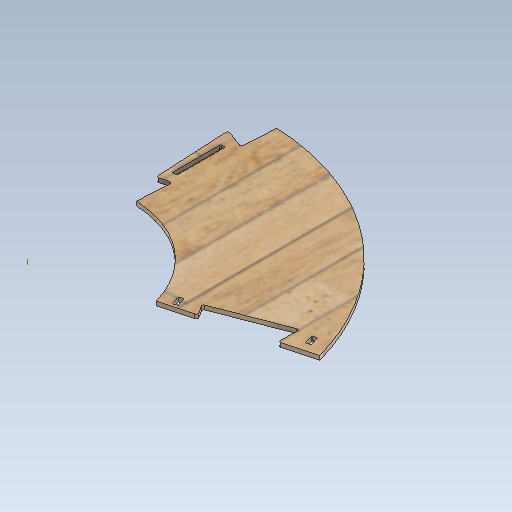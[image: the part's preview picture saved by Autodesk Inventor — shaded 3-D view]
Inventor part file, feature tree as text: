
AUTODESK INVENTOR PART (.ipt)
format: ipt  version: 2020 (Build 240168000, 168)  size: 463,360 bytes
history: native  units: mm
features: extrude x5, sketch x4, pattern_circular x3, mirror x1
ambient origin geometry x8: Origin, YZ Plane, XZ Plane, XY Plane, X Axis, Y Axis, Z Axis, Center Point
bodies: Body1 (feature_tree)
feature tree (13):
  extrude  "Extrusion3"  Depth=6.5mm
  extrude  "Extrusion4"  Depth=2.666667mm
  extrude  "Extrusion5"  Depth=1.333333mm
  sketch  "Sketch5"  dims[d32=1.333333mm d33=1.333333mm]
  extrude  "Extrusion7"  Depth=145.0mm
  pattern_circular  "Circular Pattern2"  Angle=90.0deg  [1 undecoded]
  pattern_circular  "Circular Pattern3"  [2 undecoded]
  mirror  "Mirror3"
  pattern_circular  "Circular Pattern4"  Angle=90.0deg  [1 undecoded]
  extrude  "Extrusion10"  Depth=145.0mm
  sketch  "Sketch2"  dims[d15=6.0mm d16=0.0mm d21=6.5mm]
  sketch  "Sketch3"  dims[d24=2.666667mm d25=2.666667mm]
  sketch  "Sketch6"  dims[d38=0.0mm d39=0.0mm d40=3.25mm d41=90.0deg d42=3.25mm d43=90.0deg d52=4.363323mm d54=10.0mm d55=0.0mm d60=0.872665mm d61=12.566371mm d62=13.439035mm d63=2.666667mm d64=0.523599mm d66=0.523599mm d67=2.666667mm d68=2.666667mm d70=12.566371mm d71=12.566371mm d84=300.14mm d85=682.72mm d86=491.43mm d87=150.07mm d88=341.36mm d89=4.363323mm d90=1.919862mm d91=1.919862mm d94=300.14mm d95=682.72mm d104=6.5mm d105=12.0mm d108=1.333333mm d109=1.333333mm d110=1.333333mm d111=1.333333mm d112=0.0mm d113=0.0mm d114=0.0mm d145=20.0mm d146=12.566371mm d149=145.0mm d150=90.0deg d151=90.0deg d152=90.0deg d153=90.0deg d154=20.0mm d155=25.132741mm d157=20.0mm d158=25.132741mm d169=0.0mm d170=0.0mm]
note: 4 required parameter values undecoded (feature->parameter linkage not recoverable at this tier; creation-order binding heuristic only, values carry confidence <= 0.55)
